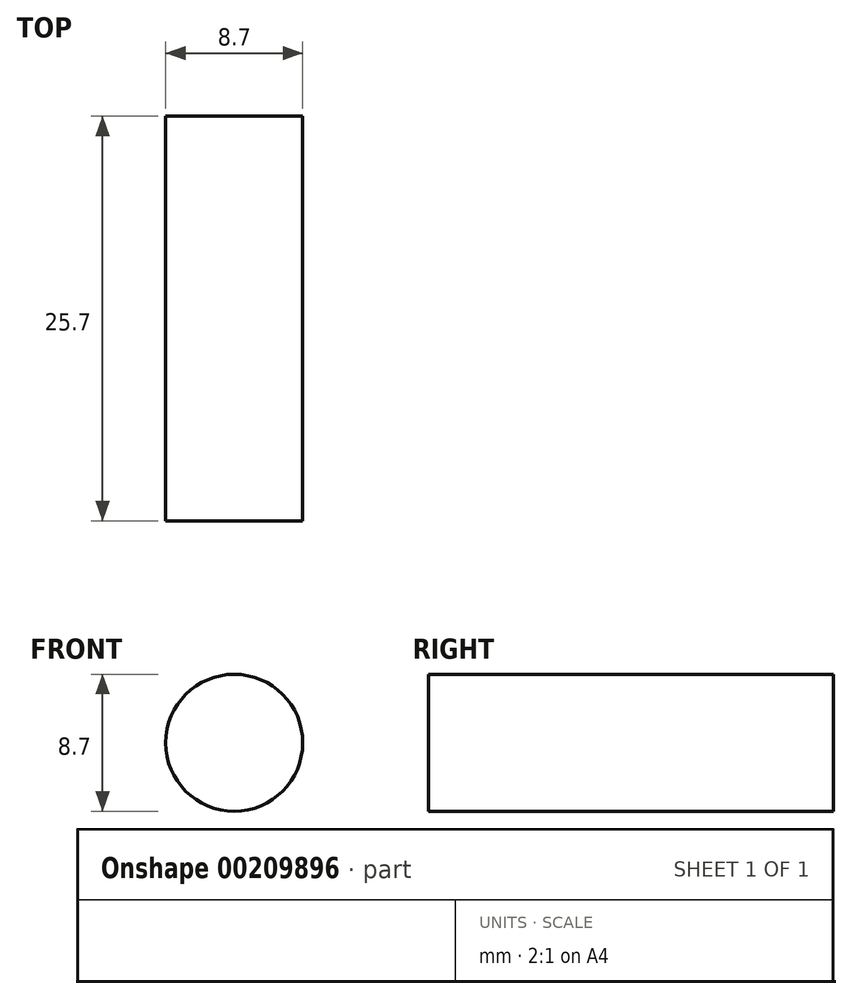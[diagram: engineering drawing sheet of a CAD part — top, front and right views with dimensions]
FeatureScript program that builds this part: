
annotation { "Feature Type Name" : "Feature", "Feature Type Description" : "" }
export const myFeature = defineFeature(function(context is Context, id is Id, definition is map)
    precondition{}
    {
        {
            var Q0;
            Q0=qCreatedBy(makeId("Front.planeOp"),FACE);
            var sketch = newSketch(context, id + "F0", { "sketchPlane" : qUnion([Q0])});
            skCircle(sketch, "E0", {"center": v(0, 0) * mm, "radius": 4.35 * mm});
            skSolve(sketch);
        }
        {
            var Q0;
            Q0=makeQuery(id+"F0.imprint","IMPRINT",FACE,{"disambiguationData":[TD([[makeQuery(id+"F0.imprint","IMPRINT",EDGE,{"derivedFrom":sQuery(id+"F0.wireOp",EDGE,"E0")}),1.0]])]});
            extrude(context, id + "F1", {"entities" : qUnion([Q0]), "depth" : 25.7 * mm});
        }
    });
